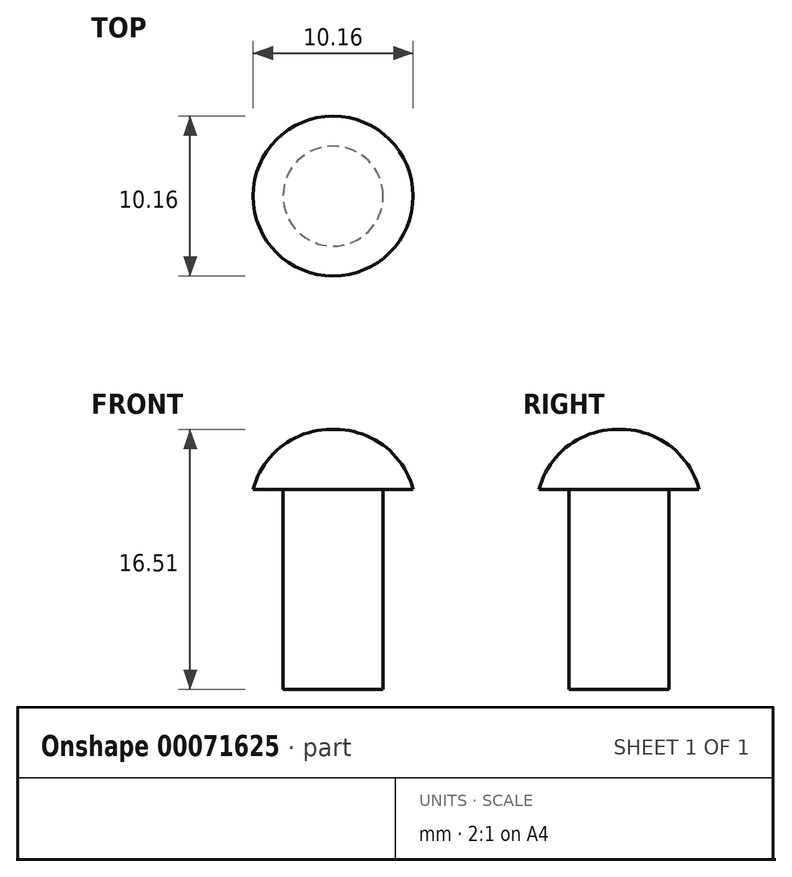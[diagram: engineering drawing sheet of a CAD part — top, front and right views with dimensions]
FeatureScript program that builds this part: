
annotation { "Feature Type Name" : "Feature", "Feature Type Description" : "" }
export const myFeature = defineFeature(function(context is Context, id is Id, definition is map)
    precondition{}
    {
        {
            var Q0;
            Q0=qCreatedBy(makeId("Top.planeOp"),FACE);
            var sketch = newSketch(context, id + "F0", { "sketchPlane" : qUnion([Q0])});
            skCircle(sketch, "E0", {"center": v(-67.74, -29.48) * mm, "radius": 3.18 * mm});
            skSolve(sketch);
        }
        {
            var Q0;
            Q0 = qSketchRegion(id + "F0", true);
            extrude(context, id + "F1", {"entities" : qUnion([Q0]), "depth" : 12.7 * mm});
        }
        {
            var Q0;
            Q0=makeQuery(id+"F1.opExtrude","CAP_FACE",FACE,{"disambiguationData":[OSD([sQuery(id+"F0.wireOp",EDGE,"E0")])],"isStart":false});
            var sketch = newSketch(context, id + "F2", { "sketchPlane" : qUnion([Q0])});
            skCircle(sketch, "E1", {"center": v(-67.74, -29.48) * mm, "radius": 5.08 * mm});
            skSolve(sketch);
        }
        {
            var Q0;
            Q0 = qSketchRegion(id + "F2", true);
            extrude(context, id + "F3", {"entities" : qUnion([Q0]), "operationType" : NewBodyOperationType.ADD, "depth" : 3.8 * mm});
        }
        {
            var Q0;
            Q0=makeQuery(id+"F3.opExtrude","CAP_FACE",FACE,{"disambiguationData":[OSD([sQuery(id+"F2.wireOp",EDGE,"E1")])],"isStart":false});
            fillet(context, id + "F4", {"entities" : qUnion([Q0]), "radius" : 5.08 * mm, "tangentPropagation" : true, "allowEdgeOverflow" : false});
        }
    });
